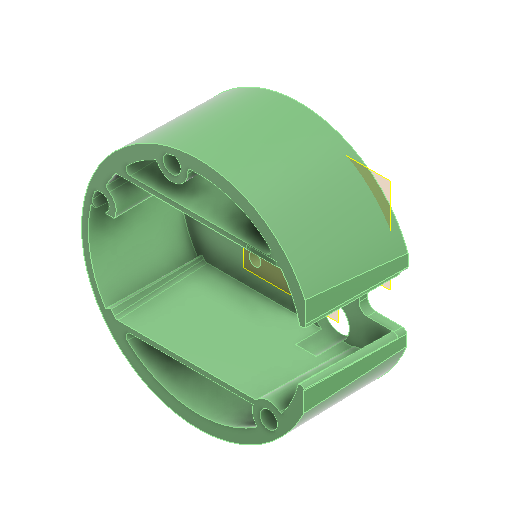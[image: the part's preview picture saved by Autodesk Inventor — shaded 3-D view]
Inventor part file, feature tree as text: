
AUTODESK INVENTOR PART (.ipt)
format: ipt  version: 2022 (Build 260153000, 153)  size: 758,784 bytes
history: native  units: in
note: dims shown in document units (in); Inventor stores cm internally (conversion verified against a paired STEP export)
features: extrude x16, sketch x16, other x9, reference x7, plane x5, projected_geometry x3, fillet x1
ambient origin geometry x8: Origin, YZ Plane, XZ Plane, XY Plane, X Axis, Y Axis, Z Axis, Center Point
bodies: Solid1 (feature_tree)
feature tree (57):
  plane  "Arbeitsebene6"
  extrude  "Extrusion1"  Depth=0.315in
  extrude  "Extrusion2"  Depth=1.0in
  plane  "Arbeitsebene3"
  extrude  "Extrusion6"  Depth=0.1102in
  plane  "Arbeitsebene2"
  extrude  "Extrusion7"  Depth=0.0787in
  extrude  "Extrusion10"  Depth=0.0394in TaperAngle=0.0deg
  plane  "Arbeitsebene7"
  sketch  "Skizze16"  dims[d81=0.0591in d82=0.3937in d83=0.0069in]
  plane  "Arbeitsebene5"
  extrude  "Extrusion14"  Depth=0.3937in
  extrude  "Extrusion15"  Depth=0.3937in
  extrude  "Extrusion17"  TaperAngle=0.0deg  [1 undecoded]
  extrude  "Extrusion18"  Depth=0.1575in
  extrude  "Extrusion19"  Depth=0.1575in
  extrude  "Extrusion20"  Depth=0.8465in TaperAngle=0.0deg
  fillet  "Rundung2"  Radius=0.1614in
  extrude  "Extrusion21"  Depth=0.1614in
  extrude  "Extrusion22"  Depth=0.315in
  extrude  "Extrusion23"  Depth=0.0069in
  extrude  "Extrusion24"  Depth=0.0394in
  extrude  "Extrusion25"  Depth=0.0069in
  sketch  "Sketch1"  dims[d0=0.0787in d1=-0.0069in d2=0.315in]
  sketch  "Sketch2"  dims[d3=0.3189in d4=1.0in d5=-0.0137in]
  sketch  "Sketch8"  dims[d33=0.1102in d34=0.1102in]
  sketch  "Sketch9"  dims[d35=0.0in d36=0.0in d37=0.0787in]
  sketch  "Skizze12"  dims[d38=0.0004in d39=-0.0069in d51=0.0394in d52=0.0in]
  sketch  "Skizze17"  dims[d89=0.3937in d90=-0.0069in d91=0.0787in]
  reference  "Referenz44"
  reference  "Referenz45"
  projected_geometry  "Projizierte Kontur4"
  sketch  "Skizze19"  dims[d92=0.0787in d93=0.0in]
  sketch  "Skizze20"  dims[d94=0.0in d104=0.1575in]
  sketch  "Skizze21"  dims[d105=0.1575in d106=0.1575in]
  sketch  "Skizze22"  dims[d107=0.0001in d108=-0.0069in d109=0.8465in d110=0.0in d111=0.1614in]
  reference  "Referenz46"
  sketch  "Skizze23"  dims[d112=0.1614in d113=0.1614in]
  sketch  "Skizze24"  dims[d114=0.1969in d115=-0.0069in d116=0.315in]
  projected_geometry  "Projizierte Kontur5"
  reference  "Referenz47"
  sketch  "Skizze25"  dims[d117=0.315in d118=0.0069in]
  reference  "Referenz48"
  reference  "Referenz49"
  reference  "Referenz50"
  sketch  "Skizze26"  dims[d119=0.0394in d120=0.0394in]
  sketch  "Skizze27"  dims[d122=0.9055in d123=0.4528in d124=1.8701in d125=0.2756in d126=0.4724in d127=0.5906in d128=0.0394in d129=0.0in d130=0.315in d131=0.315in d132=0.1102in d133=0.1102in d134=0.0in d135=0.0in d136=1.4961in d137=0.315in d138=0.315in d139=0.0591in d140=0.0in d141=2.1063in d142=0.3937in d143=0.0069in d144=0.0in d145=0.0069in d78=0.0197in d79=0.0344in d80=0.0197in d95=0.0197in d96=0.0344in d97=0.0197in d98=0.0344in]
  projected_geometry  "Projizierte Kontur6"
  other  "Matchboxscope_VCM_v1.iam"
  other  "Matchboxscope_bottom_v0:2"
  other  "Matchboxscope_middle2_m12VCMLens_v2:2"
  other  "Assembly_Matchboxscope_injectionmolded.iam"
  other  "IM_Matchboxscope_plate:1"
  other  "Assembly_Matchboxscope_injectionmolded_ESPectrometer.iam"
  other  "IM_Matchboxscope_plate:2"
  other  "IM_Lensholder:1"
  other  "DIN 912 - ersetzt durch DIN EN ISO 4762 M3 x 10:3"
note: 1 required parameter value undecoded (feature->parameter linkage not recoverable at this tier; creation-order binding heuristic only, values carry confidence <= 0.55)
